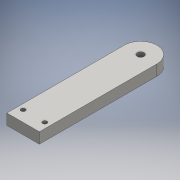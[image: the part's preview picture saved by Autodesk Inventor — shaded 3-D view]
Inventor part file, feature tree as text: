
AUTODESK INVENTOR PART (.ipt)
format: ipt  version: 2016 SP1 (Build 200210100, 210)  size: 104,960 bytes
history: native  units: mm
features: extrude x1, sketch x1
ambient origin geometry x8: Origin, YZ Plane, XZ Plane, XY Plane, X Axis, Y Axis, Z Axis, Center Point
bodies: Solid1 (feature_tree)
feature tree (2):
  extrude  "Extrusion1"  Depth=15.0mm
  sketch  "Sketch1"  dims[d0=125.0mm d1=30.0mm d2=62.5mm d3=15.0mm d4=6.4mm d5=15.0mm d6=10.0mm d7=4.0mm d8=4.0mm d9=5.0mm d10=10.0mm d11=10.0mm d12=5.0mm d13=10.0mm d14=0.0mm]
